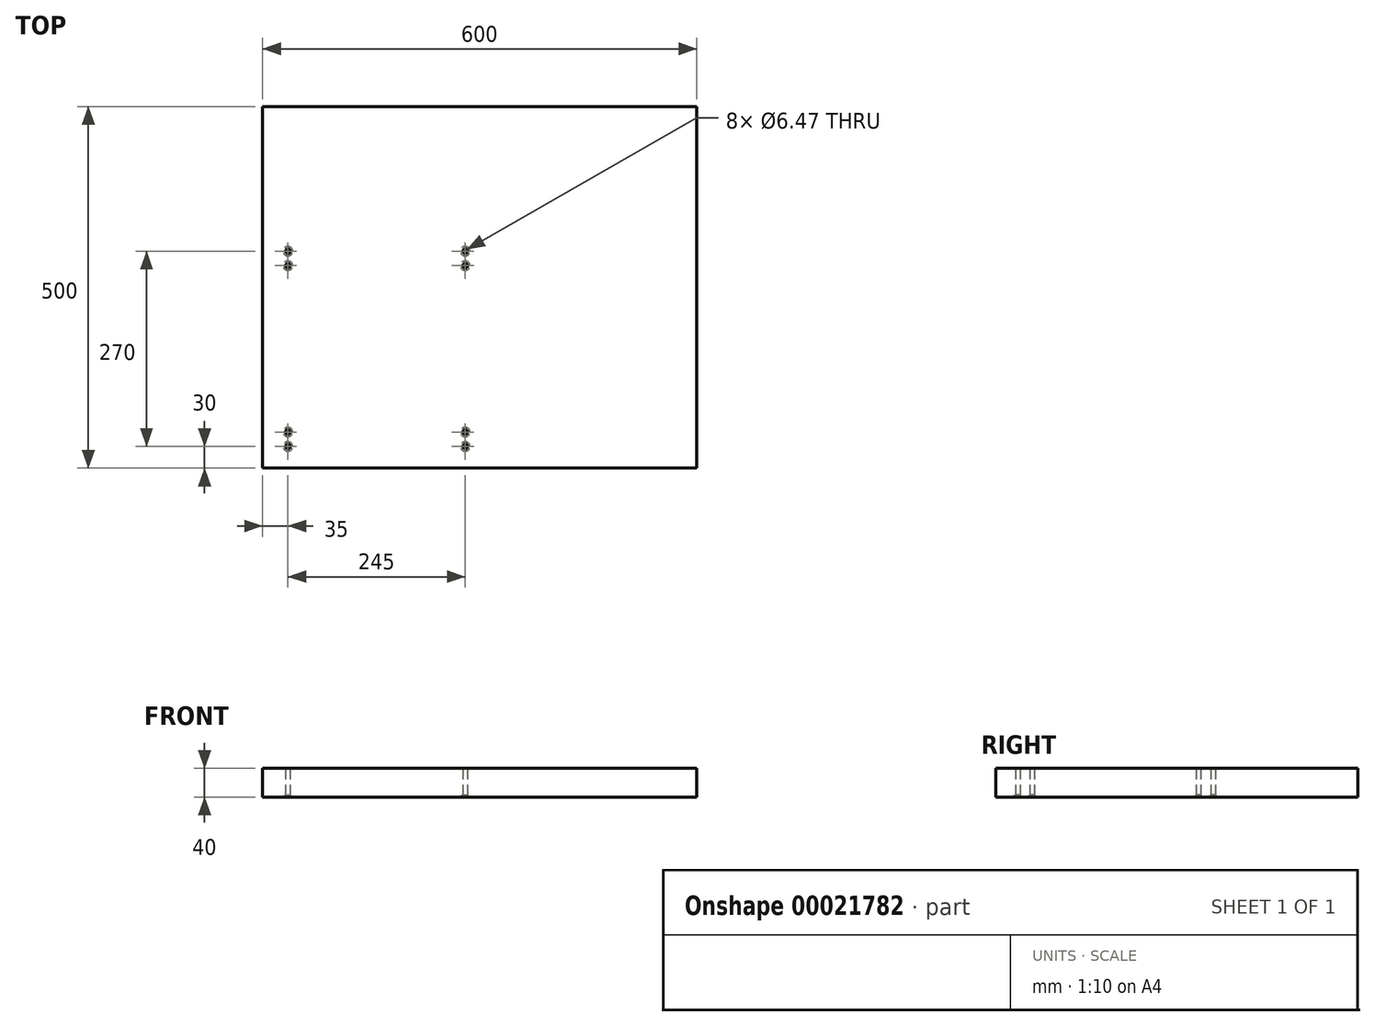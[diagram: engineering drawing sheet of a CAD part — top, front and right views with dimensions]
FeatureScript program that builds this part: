
annotation { "Feature Type Name" : "Feature", "Feature Type Description" : "" }
export const myFeature = defineFeature(function(context is Context, id is Id, definition is map)
    precondition{}
    {
        {
            var Q0;
            Q0=qCreatedBy(makeId("Top.planeOp"),FACE);
            var sketch = newSketch(context, id + "F0", { "sketchPlane" : qUnion([Q0])});
            skLineSegment(sketch, "E0.bottom", {"start": v(-300, -250) * mm, "end": v(300, -250) * mm});
            skLineSegment(sketch, "E0.top", {"start": v(-300, 250) * mm, "end": v(300, 250) * mm});
            skLineSegment(sketch, "E0.left", {"start": v(-300, -250) * mm, "end": v(-300, 250) * mm});
            skLineSegment(sketch, "E0.right", {"start": v(300, -250) * mm, "end": v(300, 250) * mm});
            skSolve(sketch);
        }
        {
            var Q0;
            Q0 = qSketchRegion(id + "F0", true);
            extrude(context, id + "F1", {"entities" : qUnion([Q0]), "depth" : 40 * mm});
        }
        {
            var Q0;
            Q0=makeQuery(id+"F0.imprint","IMPRINT",FACE,{"disambiguationData":[TD([[makeQuery(id+"F0.imprint","IMPRINT",EDGE,{"derivedFrom":sQuery(id+"F0.wireOp",EDGE,"E0.bottom")}),1.0]])]});
            var sketch = newSketch(context, id + "F2", { "sketchPlane" : qUnion([Q0])});
            skPoint(sketch, "E1", {"position": v(-265, 50) * mm});
            skPoint(sketch, "E2", {"position": v(-265, 30) * mm});
            skPoint(sketch, "E3", {"position": v(-265, -200) * mm});
            skPoint(sketch, "E4", {"position": v(-265, -220) * mm});
            skPoint(sketch, "E5", {"position": v(-20, -220) * mm});
            skPoint(sketch, "E6", {"position": v(-20, -200) * mm});
            skPoint(sketch, "E7", {"position": v(-20, 50) * mm});
            skPoint(sketch, "E8", {"position": v(-20, 30) * mm});
            skSolve(sketch);
        }
        {
            var Q0;
            Q0=sQuery(id+"F2.wireOp",VERTEX,"E5");
            var Q1;
            Q1=sQuery(id+"F2.wireOp",VERTEX,"E6");
            var Q2;
            Q2=sQuery(id+"F2.wireOp",VERTEX,"E8");
            var Q3;
            Q3=sQuery(id+"F2.wireOp",VERTEX,"E7");
            var Q4;
            Q4=sQuery(id+"F2.wireOp",VERTEX,"E1");
            var Q5;
            Q5=sQuery(id+"F2.wireOp",VERTEX,"E2");
            var Q6;
            Q6=sQuery(id+"F2.wireOp",VERTEX,"E3");
            var Q7;
            Q7=sQuery(id+"F2.wireOp",VERTEX,"E4");
            var Q8;
            Q8=makeQuery(id+"F1.opExtrude","SWEPT_BODY",BODY,{"disambiguationData":[OSD([sQuery(id+"F0.wireOp",EDGE,"E0.bottom"),sQuery(id+"F0.wireOp",EDGE,"E0.top"),sQuery(id+"F0.wireOp",EDGE,"E0.left"),sQuery(id+"F0.wireOp",EDGE,"E0.right")])]});
            hole(context, id + "F3", {"style" : HoleStyle.C_SINK, "holeDiameter" : 6.47 * mm, "cSinkDiameter" : 13 * mm, "endStyle" : HoleEndStyle.THROUGH, "oppositeDirection" : true, "locations" : qUnion([Q0, Q1, Q2, Q3, Q4, Q5, Q6, Q7]), "scope" : qUnion([Q8]), "cSinkAngle" : 90 * degree});
        }
    });
